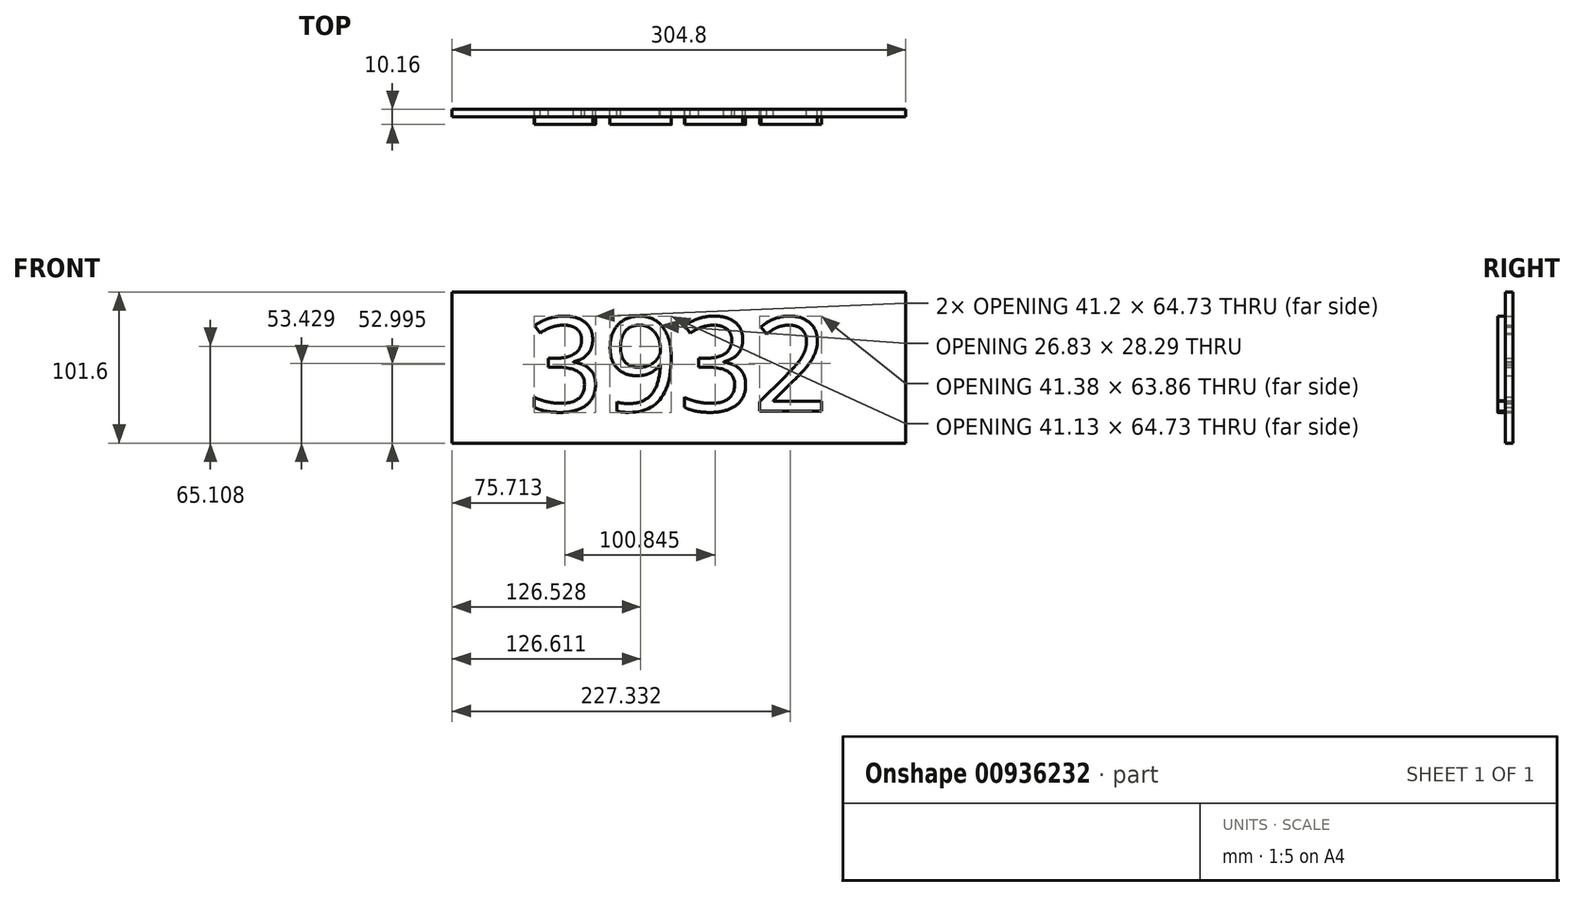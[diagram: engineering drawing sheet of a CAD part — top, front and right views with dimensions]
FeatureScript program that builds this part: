
annotation { "Feature Type Name" : "Feature", "Feature Type Description" : "" }
export const myFeature = defineFeature(function(context is Context, id is Id, definition is map)
    precondition{}
    {
        {
            var Q0;
            Q0=qCreatedBy(makeId("Front.planeOp"),FACE);
            var sketch = newSketch(context, id + "F0", { "sketchPlane" : qUnion([Q0])});
            skText(sketch, "E0", { "text": "3932\n", "fontName": "OpenSans-Regular.ttf"});
            skLineSegment(sketch, "E1.bottom", {"start": v(152.4, 50.8) * mm, "end": v(-152.4, 50.8) * mm});
            skLineSegment(sketch, "E1.top", {"start": v(152.4, -50.8) * mm, "end": v(-152.4, -50.8) * mm});
            skLineSegment(sketch, "E1.left", {"start": v(152.4, 50.8) * mm, "end": v(152.4, -50.8) * mm});
            skLineSegment(sketch, "E1.right", {"start": v(-152.4, 50.8) * mm, "end": v(-152.4, -50.8) * mm});
            skPoint(sketch, "E1.middle", {"position": v(0, 0) * mm});
            const initialGuessF0  = {"E0": [-0.10134, -0.0293, 1, 0, 0.0635]};
            skSetInitialGuess(sketch, initialGuessF0);
            skSolve(sketch);
        }
        {
            var Q0;
            Q0=makeQuery(id+"F0.imprint","IMPRINT",FACE,{"disambiguationData":[TD([[makeQuery(id+"F0.imprint","IMPRINT",EDGE,{"derivedFrom":sQuery(id+"F0.wireOp",EDGE,"E0.sketch_text.stroke-54")}),-1.0]])]});
            var Q1;
            Q1=makeQuery(id+"F0.imprint","IMPRINT",FACE,{"disambiguationData":[TD([[makeQuery(id+"F0.imprint","IMPRINT",EDGE,{"derivedFrom":sQuery(id+"F0.wireOp",EDGE,"E0.sketch_text.stroke-0")}),-1.0]])]});
            var Q2;
            Q2=makeQuery(id+"F0.imprint","IMPRINT",FACE,{"disambiguationData":[TD([[makeQuery(id+"F0.imprint","IMPRINT",EDGE,{"derivedFrom":sQuery(id+"F0.wireOp",EDGE,"E0.sketch_text.stroke-28")}),-1.0]])]});
            var Q3;
            Q3=makeQuery(id+"F0.imprint","IMPRINT",FACE,{"disambiguationData":[TD([[makeQuery(id+"F0.imprint","IMPRINT",EDGE,{"derivedFrom":sQuery(id+"F0.wireOp",EDGE,"E0.sketch_text.stroke-82")}),-1.0]])]});
            extrude(context, id + "F1", {"entities" : qUnion([Q0, Q1, Q2, Q3]), "depth" : 10.16 * mm, "offsetDistance" : 25.4 * mm});
        }
        {
            var Q0;
            Q0=makeQuery(id+"F0.imprint","IMPRINT",FACE,{"disambiguationData":[TD([[makeQuery(id+"F0.imprint","IMPRINT",EDGE,{"derivedFrom":sQuery(id+"F0.wireOp",EDGE,"E0.sketch_text.stroke-0")}),1.0]])]});
            var Q1;
            Q1=makeQuery(id+"F0.imprint","IMPRINT",FACE,{"disambiguationData":[TD([[makeQuery(id+"F0.imprint","IMPRINT",EDGE,{"derivedFrom":sQuery(id+"F0.wireOp",EDGE,"E0.sketch_text.stroke-44")}),1.0]])]});
            extrude(context, id + "F2", {"entities" : qUnion([Q0, Q1]), "depth" : 5.08 * mm, "offsetDistance" : 25.4 * mm});
        }
    });
